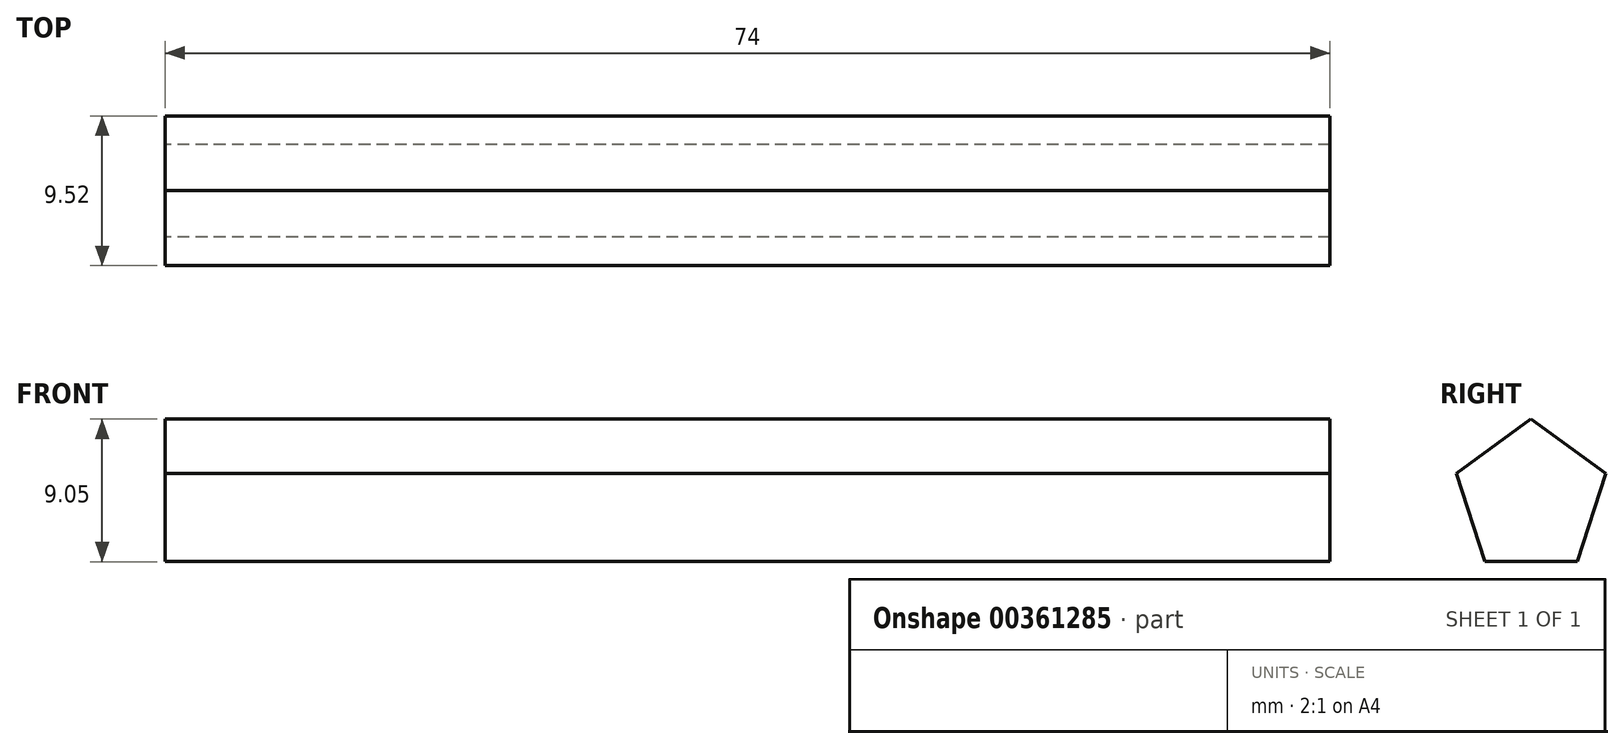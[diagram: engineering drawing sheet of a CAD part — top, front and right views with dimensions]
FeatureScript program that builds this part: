
annotation { "Feature Type Name" : "Feature", "Feature Type Description" : "" }
export const myFeature = defineFeature(function(context is Context, id is Id, definition is map)
    precondition{}
    {
        {
            var Q0;
            Q0=qCreatedBy(makeId("Right.planeOp"),FACE);
            var sketch = newSketch(context, id + "F0", { "sketchPlane" : qUnion([Q0])});
            skCircle(sketch, "E0.cCircle", {"center": v(0, 0) * mm, "radius": 4.05 * mm, "construction": true});
            skLineSegment(sketch, "E0.0", {"start": v(4.76, 1.55) * mm, "end": v(2.94, -4.05) * mm});
            skLineSegment(sketch, "E0.1", {"start": v(2.94, -4.05) * mm, "end": v(-2.94, -4.05) * mm});
            skLineSegment(sketch, "E0.2", {"start": v(-2.94, -4.05) * mm, "end": v(-4.76, 1.55) * mm});
            skLineSegment(sketch, "E0.3", {"start": v(-4.76, 1.55) * mm, "end": v(0, 5) * mm});
            skLineSegment(sketch, "E0.4", {"start": v(0, 5) * mm, "end": v(4.76, 1.55) * mm});
            skPoint(sketch, "E0.0.midPoint", {"position": v(3.85, -1.25) * mm});
            skSolve(sketch);
        }
        {
            var Q0;
            Q0=makeQuery(id+"F0.imprint","IMPRINT",FACE,{"disambiguationData":[TD([[makeQuery(id+"F0.imprint","IMPRINT",EDGE,{"derivedFrom":sQuery(id+"F0.wireOp",EDGE,"E0.0")}),-1.0]])]});
            extrude(context, id + "F1", {"entities" : qUnion([Q0]), "endBound" : BoundingType.SYMMETRIC, "depth" : 74 * mm});
        }
    });
